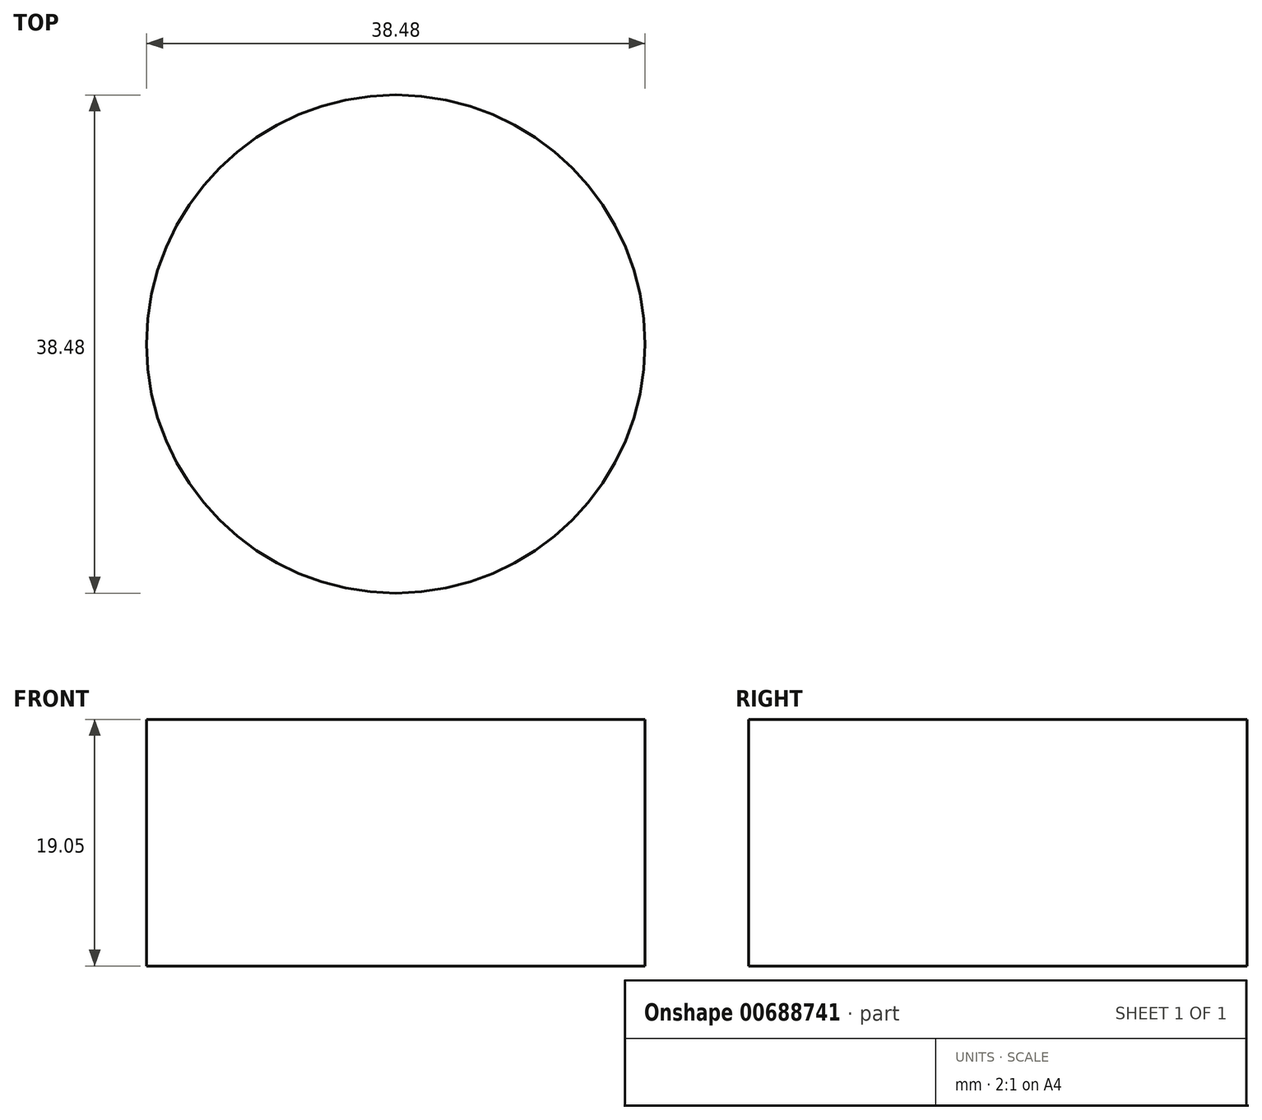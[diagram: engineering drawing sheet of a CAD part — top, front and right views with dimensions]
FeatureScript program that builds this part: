
annotation { "Feature Type Name" : "Feature", "Feature Type Description" : "" }
export const myFeature = defineFeature(function(context is Context, id is Id, definition is map)
    precondition{}
    {
        {
            var Q0;
            Q0=qCreatedBy(makeId("Top.planeOp"),FACE);
            var sketch = newSketch(context, id + "F0", { "sketchPlane" : qUnion([Q0])});
            skCircle(sketch, "E0", {"center": v(0, 0) * mm, "radius": 19.24 * mm});
            skSolve(sketch);
        }
        {
            var Q0;
            Q0=makeQuery(id+"F0.imprint","IMPRINT",FACE,{"disambiguationData":[TD([[makeQuery(id+"F0.imprint","IMPRINT",EDGE,{"derivedFrom":sQuery(id+"F0.wireOp",EDGE,"E0")}),1.0]])]});
            extrude(context, id + "F1", {"entities" : qUnion([Q0]), "oppositeDirection" : true, "depth" : 19.05 * mm, "offsetDistance" : 25.4 * mm});
        }
    });
